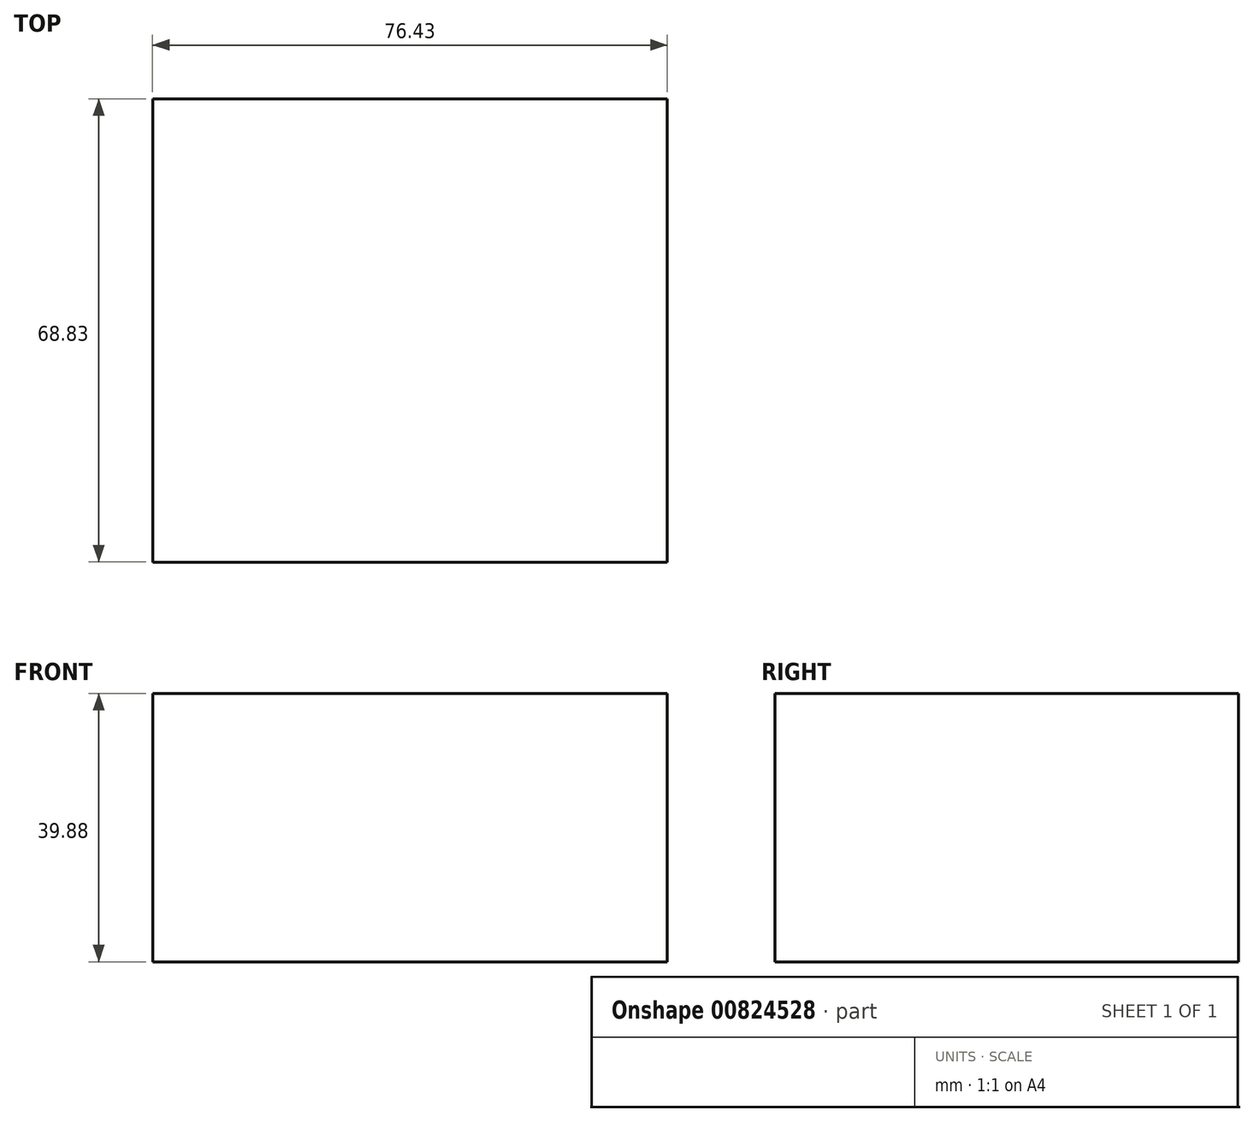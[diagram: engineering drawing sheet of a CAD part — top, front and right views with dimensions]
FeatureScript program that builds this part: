
annotation { "Feature Type Name" : "Feature", "Feature Type Description" : "" }
export const myFeature = defineFeature(function(context is Context, id is Id, definition is map)
    precondition{}
    {
        {
            var Q0;
            Q0=qCreatedBy(makeId("Top.planeOp"),FACE);
            var sketch = newSketch(context, id + "F0", { "sketchPlane" : qUnion([Q0])});
            skLineSegment(sketch, "E0.bottom", {"start": v(125.51, -44.2) * mm, "end": v(201.94, -44.2) * mm});
            skLineSegment(sketch, "E0.top", {"start": v(125.51, 24.64) * mm, "end": v(201.94, 24.64) * mm});
            skLineSegment(sketch, "E0.left", {"start": v(125.51, -44.2) * mm, "end": v(125.51, 24.64) * mm});
            skLineSegment(sketch, "E0.right", {"start": v(201.94, -44.2) * mm, "end": v(201.94, 24.64) * mm});
            skSolve(sketch);
        }
        {
            var Q0;
            Q0=makeQuery(id+"F0.imprint","IMPRINT",FACE,{"disambiguationData":[TD([[makeQuery(id+"F0.imprint","IMPRINT",EDGE,{"derivedFrom":sQuery(id+"F0.wireOp",EDGE,"E0.bottom")}),1.0]])]});
            extrude(context, id + "F1", {"entities" : qUnion([Q0]), "oppositeDirection" : true, "depth" : 39.88 * mm, "offsetDistance" : 25.4 * mm});
        }
    });
